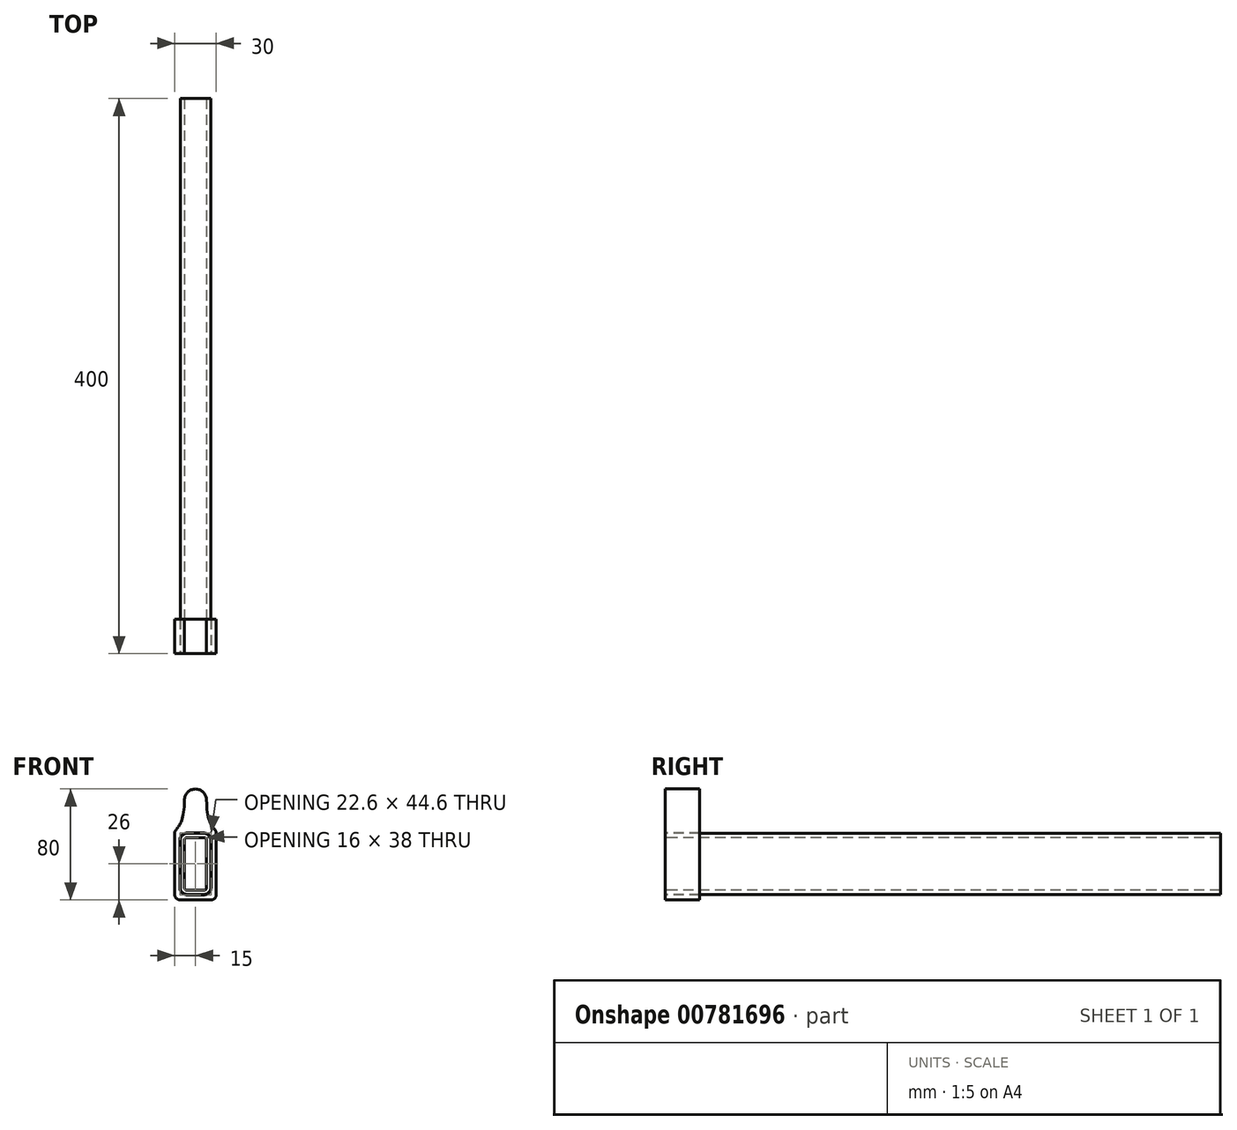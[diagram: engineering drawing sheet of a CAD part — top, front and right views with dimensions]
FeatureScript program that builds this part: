
annotation { "Feature Type Name" : "Feature", "Feature Type Description" : "" }
export const myFeature = defineFeature(function(context is Context, id is Id, definition is map)
    precondition{}
    {
        {
            var Q0;
            Q0=qCreatedBy(makeId("Front.planeOp"),FACE);
            var sketch = newSketch(context, id + "F0", { "sketchPlane" : qUnion([Q0])});
            skLineSegment(sketch, "E0.bottom", {"start": v(-6, 22) * mm, "end": v(6, 22) * mm});
            skLineSegment(sketch, "E0.top", {"start": v(-6, -22) * mm, "end": v(6, -22) * mm});
            skLineSegment(sketch, "E0.left", {"start": v(-11, 17) * mm, "end": v(-11, -17) * mm});
            skLineSegment(sketch, "E0.right", {"start": v(11, 17) * mm, "end": v(11, -17) * mm});
            skPoint(sketch, "E1.visualSharp", {"position": v(-11, 22) * mm});
            skArc(sketch, "E1.filletArc", {"start": v(-6, 22) * mm, "mid": v(-9.54, 20.54) * mm, "end": v(-11, 17) * mm});
            skPoint(sketch, "E2.visualSharp", {"position": v(11, 22) * mm});
            skArc(sketch, "E2.filletArc", {"start": v(11, 17) * mm, "mid": v(9.54, 20.54) * mm, "end": v(6, 22) * mm});
            skPoint(sketch, "E3.visualSharp", {"position": v(11, -22) * mm});
            skArc(sketch, "E3.filletArc", {"start": v(6, -22) * mm, "mid": v(9.54, -20.54) * mm, "end": v(11, -17) * mm});
            skPoint(sketch, "E4.visualSharp", {"position": v(-11, -22) * mm});
            skArc(sketch, "E4.filletArc", {"start": v(-11, -17) * mm, "mid": v(-9.54, -20.54) * mm, "end": v(-6, -22) * mm});
            skLineSegment(sketch, "E5", {"start": v(-11, 0) * mm, "end": v(11, 0) * mm, "construction": true});
            skLineSegment(sketch, "E6.0", {"start": v(-6, 19) * mm, "end": v(6, 19) * mm});
            skArc(sketch, "E6.1", {"start": v(8, 17) * mm, "mid": v(7.41, 18.41) * mm, "end": v(6, 19) * mm});
            skArc(sketch, "E6.2", {"start": v(-6, 19) * mm, "mid": v(-7.41, 18.41) * mm, "end": v(-8, 17) * mm});
            skLineSegment(sketch, "E6.3", {"start": v(8, 17) * mm, "end": v(8, -17) * mm});
            skLineSegment(sketch, "E6.4", {"start": v(-8, 17) * mm, "end": v(-8, -17) * mm});
            skArc(sketch, "E6.5", {"start": v(-8, -17) * mm, "mid": v(-7.41, -18.41) * mm, "end": v(-6, -19) * mm});
            skLineSegment(sketch, "E6.6", {"start": v(-6, -19) * mm, "end": v(6, -19) * mm});
            skArc(sketch, "E6.7", {"start": v(6, -19) * mm, "mid": v(7.41, -18.41) * mm, "end": v(8, -17) * mm});
            skSolve(sketch);
        }
        {
            var Q0;
            Q0 = qSketchRegion(id + "F0", true);
            extrude(context, id + "F1", {"entities" : qUnion([Q0]), "oppositeDirection" : true, "depth" : 400 * mm, "offsetDistance" : 25 * mm});
        }
        {
            var Q0;
            Q0=qCreatedBy(makeId("Front.planeOp"),FACE);
            var sketch = newSketch(context, id + "F2", { "sketchPlane" : qUnion([Q0])});
            skLineSegment(sketch, "E7", {"start": v(-15, 26) * mm, "end": v(-15, -26) * mm, "construction": true});
            skLineSegment(sketch, "E8", {"start": v(-11, -26) * mm, "end": v(11, -26) * mm});
            skLineSegment(sketch, "E9", {"start": v(8, 46) * mm, "end": v(-8, 46) * mm, "construction": true});
            skLineSegment(sketch, "E10", {"start": v(-8, 46) * mm, "end": v(-8, 26) * mm, "construction": true});
            skLineSegment(sketch, "E11", {"start": v(-8, 26) * mm, "end": v(-15, 26) * mm, "construction": true});
            skLineSegment(sketch, "E12", {"start": v(0, 0) * mm, "end": v(0, 46) * mm, "construction": true});
            skArc(sketch, "E13.0", {"start": v(11.3, 17) * mm, "mid": v(9.75, 20.75) * mm, "end": v(6, 22.3) * mm});
            skLineSegment(sketch, "E13.1", {"start": v(-6, 22.3) * mm, "end": v(6, 22.3) * mm});
            skLineSegment(sketch, "E13.2", {"start": v(11.3, 17) * mm, "end": v(11.3, -17) * mm});
            skArc(sketch, "E13.3", {"start": v(-6, 22.3) * mm, "mid": v(-9.75, 20.75) * mm, "end": v(-11.3, 17) * mm});
            skArc(sketch, "E13.4", {"start": v(6, -22.3) * mm, "mid": v(9.75, -20.75) * mm, "end": v(11.3, -17) * mm});
            skLineSegment(sketch, "E13.5", {"start": v(-6, -22.3) * mm, "end": v(6, -22.3) * mm});
            skArc(sketch, "E13.6", {"start": v(-11.3, -17) * mm, "mid": v(-9.75, -20.75) * mm, "end": v(-6, -22.3) * mm});
            skLineSegment(sketch, "E13.7", {"start": v(-11.3, 17) * mm, "end": v(-11.3, -17) * mm});
            skCircle(sketch, "E14", {"center": v(0, 46) * mm, "radius": 4 * mm, "construction": true});
            skArc(sketch, "E15", {"start": v(8, 46) * mm, "mid": v(0, 54) * mm, "end": v(-8, 46) * mm});
            skFitSpline(sketch, "E16", {"points": [v(-15, 22.3) * mm, v(-8, 46) * mm], "startDerivative": vector(0, 11.1) * mm, "endDerivative": vector(0, 60) * mm});
            skLineSegment(sketch, "E17", {"start": v(-15, 22.3) * mm, "end": v(-15, -22) * mm});
            skFitSpline(sketch, "E18.MirrorCS", {"points": [v(15, 22.3) * mm, v(8, 46) * mm], "startDerivative": vector(0, 11.1) * mm, "endDerivative": vector(0, 60) * mm});
            skLineSegment(sketch, "E19", {"start": v(15, -22) * mm, "end": v(15, 22.3) * mm});
            skPoint(sketch, "E20.visualSharp", {"position": v(15, -26) * mm});
            skArc(sketch, "E20.filletArc", {"start": v(11, -26) * mm, "mid": v(13.83, -24.83) * mm, "end": v(15, -22) * mm});
            skPoint(sketch, "E21.visualSharp", {"position": v(-15, -26) * mm});
            skArc(sketch, "E21.filletArc", {"start": v(-15, -22) * mm, "mid": v(-13.83, -24.83) * mm, "end": v(-11, -26) * mm});
            skSolve(sketch);
        }
        {
            var Q0;
            Q0 = qSketchRegion(id + "F2", true);
            extrude(context, id + "F3", {"entities" : qUnion([Q0]), "oppositeDirection" : true, "depth" : 25 * mm, "offsetDistance" : 25 * mm});
        }
    });
